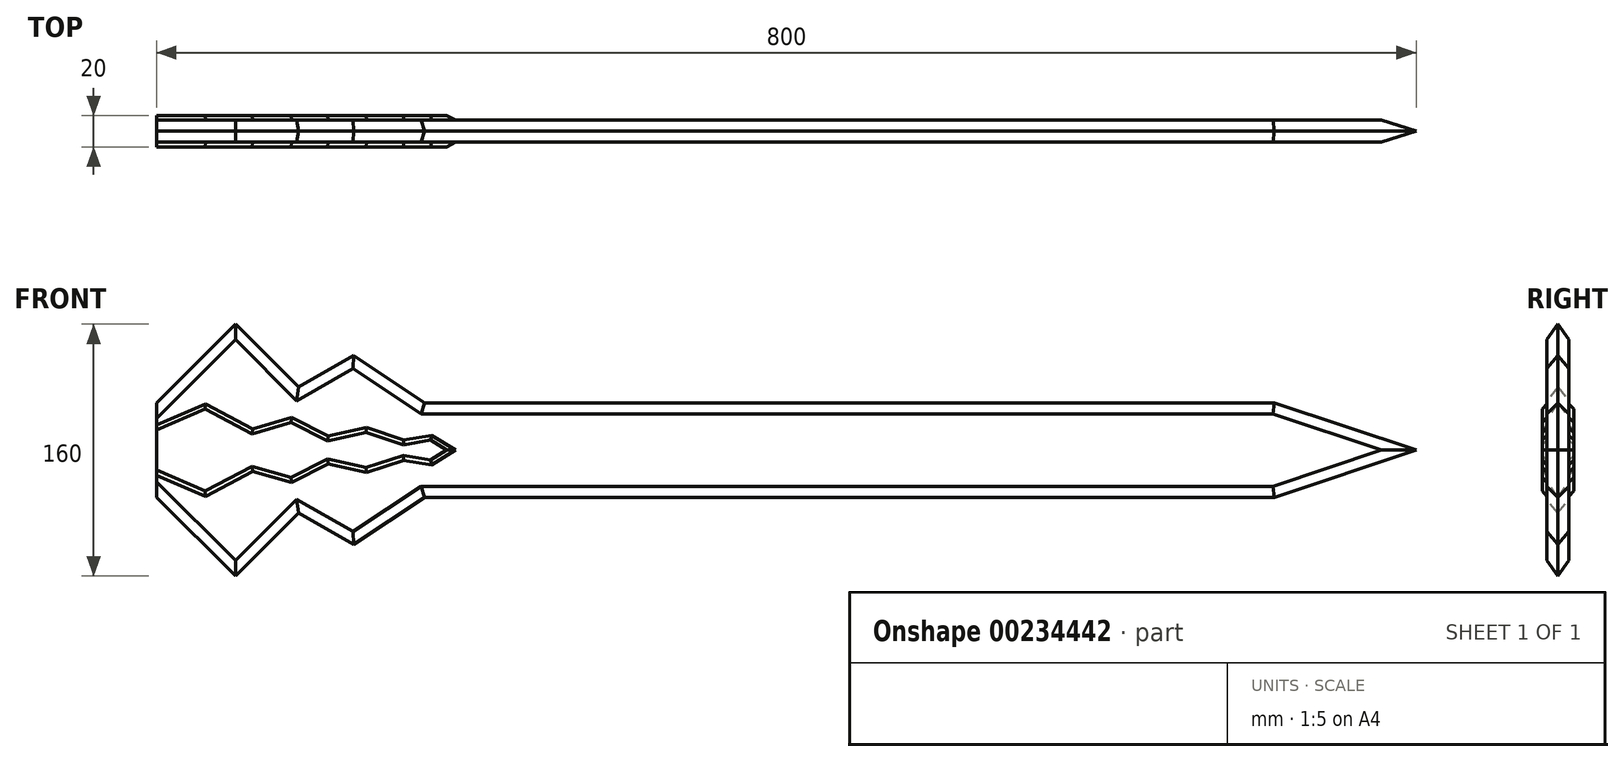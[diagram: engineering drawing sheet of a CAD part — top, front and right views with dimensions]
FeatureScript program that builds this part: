
annotation { "Feature Type Name" : "Feature", "Feature Type Description" : "" }
export const myFeature = defineFeature(function(context is Context, id is Id, definition is map)
    precondition{}
    {
        {
            var Q0;
            Q0=qCreatedBy(makeId("Front.planeOp"),FACE);
            var sketch = newSketch(context, id + "F0", { "sketchPlane" : qUnion([Q0])});
            skLineSegment(sketch, "E0", {"start": v(0, 0) * mm, "end": v(0, 30) * mm});
            skLineSegment(sketch, "E1", {"start": v(0, 30) * mm, "end": v(50, 80) * mm});
            skLineSegment(sketch, "E2", {"start": v(50, 80) * mm, "end": v(90, 40) * mm});
            skLineSegment(sketch, "E3", {"start": v(90, 40) * mm, "end": v(125, 60) * mm});
            skLineSegment(sketch, "E4", {"start": v(125, 60) * mm, "end": v(170, 30) * mm});
            skLineSegment(sketch, "E5", {"start": v(170, 30) * mm, "end": v(710, 30) * mm});
            skLineSegment(sketch, "E6", {"start": v(710, 30) * mm, "end": v(800, 0) * mm});
            skLineSegment(sketch, "E7", {"start": v(800, 0) * mm, "end": v(0, 0) * mm});
            skLineSegment(sketch, "E8.MirrorCS", {"start": v(0, -30) * mm, "end": v(50, -80) * mm});
            skLineSegment(sketch, "E9.MirrorCS", {"start": v(170, -30) * mm, "end": v(710, -30) * mm});
            skLineSegment(sketch, "E10.MirrorCS", {"start": v(125, -60) * mm, "end": v(170, -30) * mm});
            skLineSegment(sketch, "E11.MirrorCS", {"start": v(50, -80) * mm, "end": v(90, -40) * mm});
            skLineSegment(sketch, "E12.MirrorCS", {"start": v(90, -40) * mm, "end": v(125, -60) * mm});
            skLineSegment(sketch, "E13.MirrorCS", {"start": v(0, 0) * mm, "end": v(0, -30) * mm});
            skLineSegment(sketch, "E14.MirrorCS", {"start": v(710, -30) * mm, "end": v(800, 0) * mm});
            skSolve(sketch);
        }
        {
            var Q0;
            Q0 = qSketchRegion(id + "F0", true);
            extrude(context, id + "F1", {"entities" : qUnion([Q0]), "depth" : 7 * mm});
        }
        {
            var Q0;
            Q0=makeQuery(id+"F1.opExtrude","CAP_EDGE",EDGE,{"disambiguationData":[OSD([sQuery(id+"F0.wireOp",EDGE,"E1")])],"isStart":false});
            var Q1;
            Q1=makeQuery(id+"F1.opExtrude","CAP_EDGE",EDGE,{"disambiguationData":[OSD([sQuery(id+"F0.wireOp",EDGE,"E2")])],"isStart":false});
            var Q2;
            Q2=makeQuery(id+"F1.opExtrude","CAP_EDGE",EDGE,{"disambiguationData":[OSD([sQuery(id+"F0.wireOp",EDGE,"E3")])],"isStart":false});
            var Q3;
            Q3=makeQuery(id+"F1.opExtrude","CAP_EDGE",EDGE,{"disambiguationData":[OSD([sQuery(id+"F0.wireOp",EDGE,"E4")])],"isStart":false});
            var Q4;
            Q4=makeQuery(id+"F1.opExtrude","CAP_EDGE",EDGE,{"disambiguationData":[OSD([sQuery(id+"F0.wireOp",EDGE,"E5")])],"isStart":false});
            var Q5;
            Q5=makeQuery(id+"F1.opExtrude","CAP_EDGE",EDGE,{"disambiguationData":[OSD([sQuery(id+"F0.wireOp",EDGE,"E6")])],"isStart":false});
            var Q6;
            Q6=makeQuery(id+"F1.opExtrude","CAP_EDGE",EDGE,{"disambiguationData":[OSD([sQuery(id+"F0.wireOp",EDGE,"E8.MirrorCS")])],"isStart":false});
            var Q7;
            Q7=makeQuery(id+"F1.opExtrude","CAP_EDGE",EDGE,{"disambiguationData":[OSD([sQuery(id+"F0.wireOp",EDGE,"E11.MirrorCS")])],"isStart":false});
            var Q8;
            Q8=makeQuery(id+"F1.opExtrude","CAP_EDGE",EDGE,{"disambiguationData":[OSD([sQuery(id+"F0.wireOp",EDGE,"E12.MirrorCS")])],"isStart":false});
            var Q9;
            Q9=makeQuery(id+"F1.opExtrude","CAP_EDGE",EDGE,{"disambiguationData":[OSD([sQuery(id+"F0.wireOp",EDGE,"E10.MirrorCS")])],"isStart":false});
            var Q10;
            Q10=makeQuery(id+"F1.opExtrude","CAP_EDGE",EDGE,{"disambiguationData":[OSD([sQuery(id+"F0.wireOp",EDGE,"E9.MirrorCS")])],"isStart":false});
            var Q11;
            Q11=makeQuery(id+"F1.opExtrude","CAP_EDGE",EDGE,{"disambiguationData":[OSD([sQuery(id+"F0.wireOp",EDGE,"E14.MirrorCS")])],"isStart":false});
            chamfer(context, id + "F2", {"entities" : qUnion([Q0, Q1, Q2, Q3, Q4, Q5, Q6, Q7, Q8, Q9, Q10, Q11]), "width" : 7 * mm, "tangentPropagation" : true});
        }
        {
            var Q0;
            Q0=makeQuery(id+"F1.opExtrude","CAP_FACE",FACE,{"disambiguationData":[OSD([sQuery(id+"F0.wireOp",EDGE,"E0"),sQuery(id+"F0.wireOp",EDGE,"E6"),sQuery(id+"F0.wireOp",EDGE,"E3"),sQuery(id+"F0.wireOp",EDGE,"E2"),sQuery(id+"F0.wireOp",EDGE,"E4"),sQuery(id+"F0.wireOp",EDGE,"E5"),sQuery(id+"F0.wireOp",EDGE,"E1"),sQuery(id+"F0.wireOp",EDGE,"E13.MirrorCS"),sQuery(id+"F0.wireOp",EDGE,"E10.MirrorCS"),sQuery(id+"F0.wireOp",EDGE,"E9.MirrorCS"),sQuery(id+"F0.wireOp",EDGE,"E8.MirrorCS"),sQuery(id+"F0.wireOp",EDGE,"E14.MirrorCS"),sQuery(id+"F0.wireOp",EDGE,"E12.MirrorCS"),sQuery(id+"F0.wireOp",EDGE,"E11.MirrorCS")])],"isStart":false});
            var sketch = newSketch(context, id + "F3", { "sketchPlane" : qUnion([Q0])});
            skLineSegment(sketch, "E15", {"start": v(190, 0) * mm, "end": v(0, 0) * mm});
            skLineSegment(sketch, "E16", {"start": v(0, 0) * mm, "end": v(0, 16.03) * mm});
            skLineSegment(sketch, "E17", {"start": v(0, 16.03) * mm, "end": v(31.06, 29.36) * mm});
            skLineSegment(sketch, "E18", {"start": v(31.06, 29.36) * mm, "end": v(60.92, 13.5) * mm});
            skLineSegment(sketch, "E19", {"start": v(60.92, 13.5) * mm, "end": v(85.8, 20.6) * mm});
            skLineSegment(sketch, "E20", {"start": v(85.8, 20.6) * mm, "end": v(108.85, 8.84) * mm});
            skLineSegment(sketch, "E21", {"start": v(108.85, 8.84) * mm, "end": v(133.2, 14.21) * mm});
            skLineSegment(sketch, "E22", {"start": v(133.2, 14.21) * mm, "end": v(156.9, 6.47) * mm});
            skLineSegment(sketch, "E23", {"start": v(156.9, 6.47) * mm, "end": v(174.66, 9.42) * mm});
            skLineSegment(sketch, "E24", {"start": v(174.66, 9.42) * mm, "end": v(190, 0) * mm});
            skLineSegment(sketch, "E25", {"start": v(60.92, 13.5) * mm, "end": v(0, 16.03) * mm});
            skLineSegment(sketch, "E26", {"start": v(60.92, 13.5) * mm, "end": v(108.85, 8.84) * mm});
            skLineSegment(sketch, "E27", {"start": v(156.9, 6.47) * mm, "end": v(108.85, 8.84) * mm});
            skLineSegment(sketch, "E28", {"start": v(156.9, 6.47) * mm, "end": v(190, 0) * mm});
            skLineSegment(sketch, "E29", {"start": v(31.06, 29.36) * mm, "end": v(30.46, 14.77) * mm});
            skLineSegment(sketch, "E30", {"start": v(85.8, 20.6) * mm, "end": v(84.88, 11.17) * mm});
            skLineSegment(sketch, "E31", {"start": v(133.2, 14.21) * mm, "end": v(132.88, 7.66) * mm});
            skLineSegment(sketch, "E32", {"start": v(174.66, 9.42) * mm, "end": v(173.45, 3.24) * mm});
            skLineSegment(sketch, "E33.MirrorCS", {"start": v(85.8, -20.6) * mm, "end": v(84.88, -11.17) * mm});
            skLineSegment(sketch, "E34.MirrorCS", {"start": v(133.2, -14.21) * mm, "end": v(132.88, -7.66) * mm});
            skLineSegment(sketch, "E35.MirrorCS", {"start": v(174.66, -9.42) * mm, "end": v(173.45, -3.24) * mm});
            skLineSegment(sketch, "E36.MirrorCS", {"start": v(31.06, -29.36) * mm, "end": v(30.46, -14.77) * mm});
            skLineSegment(sketch, "E37.MirrorCS", {"start": v(0, 0) * mm, "end": v(0, -16.03) * mm});
            skLineSegment(sketch, "E38.MirrorCS", {"start": v(156.9, -6.47) * mm, "end": v(190, 0) * mm});
            skLineSegment(sketch, "E39.MirrorCS", {"start": v(0, -16.03) * mm, "end": v(31.06, -29.36) * mm});
            skLineSegment(sketch, "E40.MirrorCS", {"start": v(31.06, -29.36) * mm, "end": v(60.92, -13.5) * mm});
            skLineSegment(sketch, "E41.MirrorCS", {"start": v(60.92, -13.5) * mm, "end": v(85.8, -20.6) * mm});
            skLineSegment(sketch, "E42.MirrorCS", {"start": v(174.66, -9.42) * mm, "end": v(190, 0) * mm});
            skLineSegment(sketch, "E43.MirrorCS", {"start": v(60.92, -13.5) * mm, "end": v(0, -16.03) * mm});
            skLineSegment(sketch, "E44.MirrorCS", {"start": v(60.92, -13.5) * mm, "end": v(108.85, -8.84) * mm});
            skLineSegment(sketch, "E45.MirrorCS", {"start": v(156.9, -6.47) * mm, "end": v(174.66, -9.42) * mm});
            skLineSegment(sketch, "E46.MirrorCS", {"start": v(85.8, -20.6) * mm, "end": v(108.85, -8.84) * mm});
            skLineSegment(sketch, "E47.MirrorCS", {"start": v(108.85, -8.84) * mm, "end": v(133.2, -14.21) * mm});
            skLineSegment(sketch, "E48.MirrorCS", {"start": v(133.2, -14.21) * mm, "end": v(156.9, -6.47) * mm});
            skLineSegment(sketch, "E49.MirrorCS", {"start": v(156.9, -6.47) * mm, "end": v(108.85, -8.84) * mm});
            skSolve(sketch);
        }
        {
            var Q0;
            Q0 = qSketchRegion(id + "F3", true);
            extrude(context, id + "F4", {"entities" : qUnion([Q0]), "operationType" : NewBodyOperationType.ADD, "depth" : 3 * mm});
        }
        {
            var Q0;
            Q0=makeQuery(id+"F4.opExtrude","CAP_EDGE",EDGE,{"disambiguationData":[OSD([sQuery(id+"F3.wireOp",EDGE,"E17")])],"isStart":false});
            var Q1;
            Q1=makeQuery(id+"F4.opExtrude","CAP_EDGE",EDGE,{"disambiguationData":[OSD([sQuery(id+"F3.wireOp",EDGE,"E18")])],"isStart":false});
            var Q2;
            Q2=makeQuery(id+"F4.opExtrude","CAP_EDGE",EDGE,{"disambiguationData":[OSD([sQuery(id+"F3.wireOp",EDGE,"E19")])],"isStart":false});
            var Q3;
            Q3=makeQuery(id+"F4.opExtrude","CAP_EDGE",EDGE,{"disambiguationData":[OSD([sQuery(id+"F3.wireOp",EDGE,"E20")])],"isStart":false});
            var Q4;
            Q4=makeQuery(id+"F4.opExtrude","CAP_EDGE",EDGE,{"disambiguationData":[OSD([sQuery(id+"F3.wireOp",EDGE,"E21")])],"isStart":false});
            var Q5;
            Q5=makeQuery(id+"F4.opExtrude","CAP_EDGE",EDGE,{"disambiguationData":[OSD([sQuery(id+"F3.wireOp",EDGE,"E22")])],"isStart":false});
            var Q6;
            Q6=makeQuery(id+"F4.opExtrude","CAP_EDGE",EDGE,{"disambiguationData":[OSD([sQuery(id+"F3.wireOp",EDGE,"E23")])],"isStart":false});
            var Q7;
            Q7=makeQuery(id+"F4.opExtrude","CAP_EDGE",EDGE,{"disambiguationData":[OSD([sQuery(id+"F3.wireOp",EDGE,"E24")])],"isStart":false});
            var Q8;
            Q8=makeQuery(id+"F4.opExtrude","CAP_EDGE",EDGE,{"disambiguationData":[OSD([sQuery(id+"F3.wireOp",EDGE,"E42.MirrorCS")])],"isStart":false});
            var Q9;
            Q9=makeQuery(id+"F4.opExtrude","CAP_EDGE",EDGE,{"disambiguationData":[OSD([sQuery(id+"F3.wireOp",EDGE,"E45.MirrorCS")])],"isStart":false});
            var Q10;
            Q10=makeQuery(id+"F4.opExtrude","CAP_EDGE",EDGE,{"disambiguationData":[OSD([sQuery(id+"F3.wireOp",EDGE,"E48.MirrorCS")])],"isStart":false});
            var Q11;
            Q11=makeQuery(id+"F4.opExtrude","CAP_EDGE",EDGE,{"disambiguationData":[OSD([sQuery(id+"F3.wireOp",EDGE,"E47.MirrorCS")])],"isStart":false});
            var Q12;
            Q12=makeQuery(id+"F4.opExtrude","CAP_EDGE",EDGE,{"disambiguationData":[OSD([sQuery(id+"F3.wireOp",EDGE,"E46.MirrorCS")])],"isStart":false});
            var Q13;
            Q13=makeQuery(id+"F4.opExtrude","CAP_EDGE",EDGE,{"disambiguationData":[OSD([sQuery(id+"F3.wireOp",EDGE,"E41.MirrorCS")])],"isStart":false});
            var Q14;
            Q14=makeQuery(id+"F4.opExtrude","CAP_EDGE",EDGE,{"disambiguationData":[OSD([sQuery(id+"F3.wireOp",EDGE,"E40.MirrorCS")])],"isStart":false});
            var Q15;
            Q15=makeQuery(id+"F4.opExtrude","CAP_EDGE",EDGE,{"disambiguationData":[OSD([sQuery(id+"F3.wireOp",EDGE,"E39.MirrorCS")])],"isStart":false});
            chamfer(context, id + "F5", {"entities" : qUnion([Q0, Q1, Q2, Q3, Q4, Q5, Q6, Q7, Q8, Q9, Q10, Q11, Q12, Q13, Q14, Q15]), "width" : 3 * mm, "tangentPropagation" : true});
        }
        {
            var Q0;
            Q0=makeQuery(id+"F1.opExtrude","SWEPT_BODY",BODY,{"disambiguationData":[OSD([sQuery(id+"F0.wireOp",EDGE,"E0"),sQuery(id+"F0.wireOp",EDGE,"E6"),sQuery(id+"F0.wireOp",EDGE,"E3"),sQuery(id+"F0.wireOp",EDGE,"E2"),sQuery(id+"F0.wireOp",EDGE,"E4"),sQuery(id+"F0.wireOp",EDGE,"E5"),sQuery(id+"F0.wireOp",EDGE,"E1"),sQuery(id+"F0.wireOp",EDGE,"E13.MirrorCS"),sQuery(id+"F0.wireOp",EDGE,"E10.MirrorCS"),sQuery(id+"F0.wireOp",EDGE,"E9.MirrorCS"),sQuery(id+"F0.wireOp",EDGE,"E8.MirrorCS"),sQuery(id+"F0.wireOp",EDGE,"E14.MirrorCS"),sQuery(id+"F0.wireOp",EDGE,"E12.MirrorCS"),sQuery(id+"F0.wireOp",EDGE,"E11.MirrorCS")])]});
            var Q1;
            Q1=qCreatedBy(makeId("Front.planeOp"),FACE);
            mirror(context, id + "F6", {"operationType" : NewBodyOperationType.ADD, "entities" : qUnion([Q0]), "mirrorPlane" : qUnion([Q1])});
        }
    });
